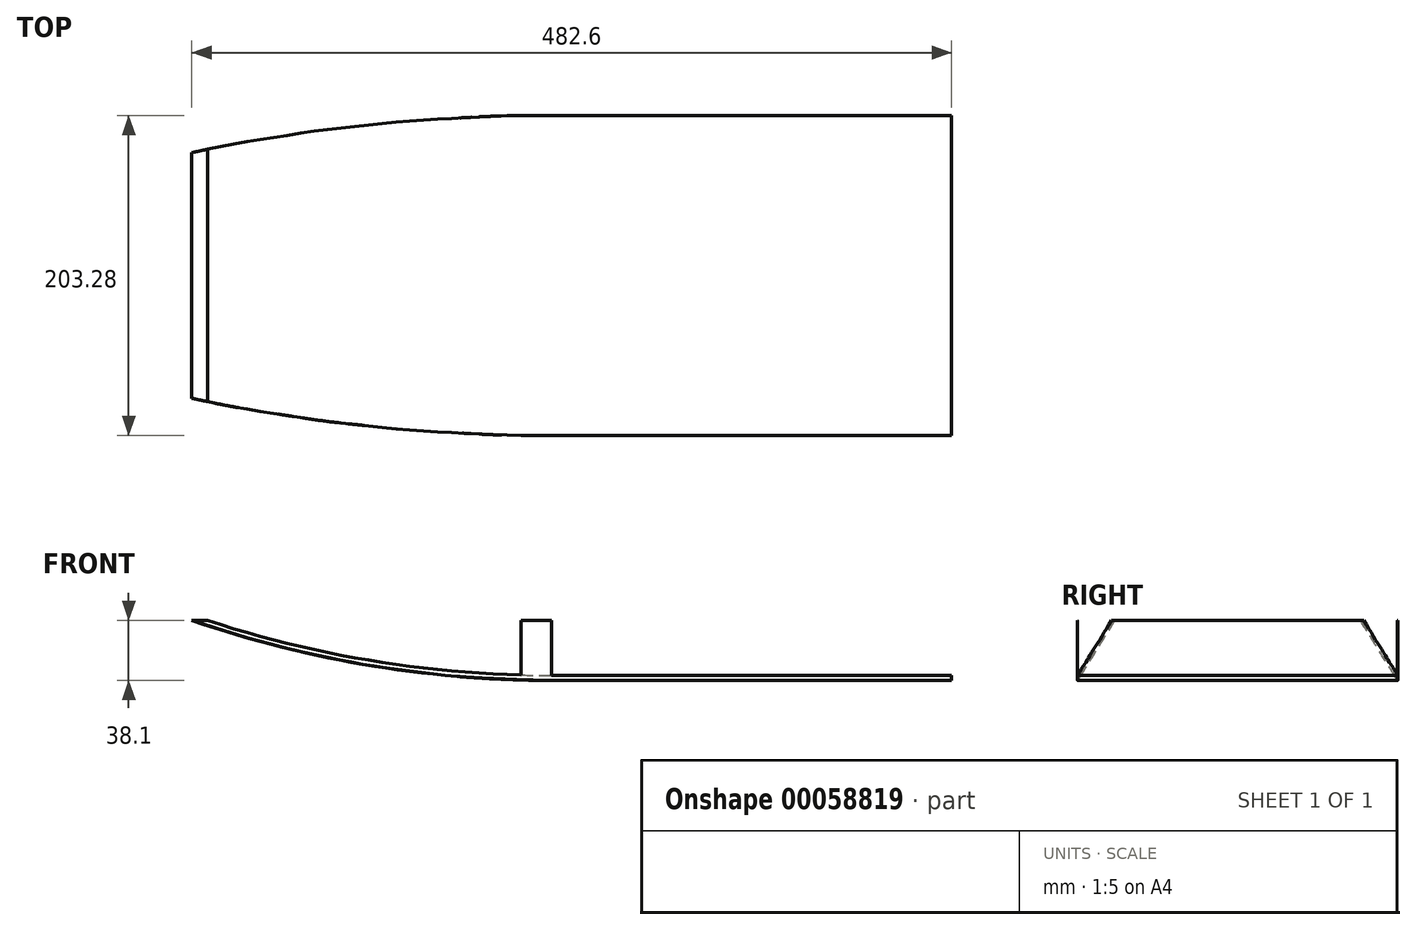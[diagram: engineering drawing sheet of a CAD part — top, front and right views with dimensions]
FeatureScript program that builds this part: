
annotation { "Feature Type Name" : "Feature", "Feature Type Description" : "" }
export const myFeature = defineFeature(function(context is Context, id is Id, definition is map)
    precondition{}
    {
        {
            var Q0;
            Q0=qCreatedBy(makeId("Front.planeOp"),FACE);
            var sketch = newSketch(context, id + "F0", { "sketchPlane" : qUnion([Q0])});
            skLineSegment(sketch, "E0.bottom", {"start": v(0, 0) * mm, "end": v(254, 0) * mm});
            skLineSegment(sketch, "E0.right", {"start": v(254, 0) * mm, "end": v(254, 38.1) * mm});
            skLineSegment(sketch, "E1", {"start": v(254, 38.1) * mm, "end": v(-228.6, 38.1) * mm});
            skArc(sketch, "E2", {"start": v(0, 0) * mm, "mid": v(-115.88, 9.6) * mm, "end": v(-228.6, 38.1) * mm});
            skSolve(sketch);
        }
        {
            var Q0;
            Q0=makeQuery(id+"F0.imprint","IMPRINT",FACE,{"disambiguationData":[TD([[makeQuery(id+"F0.imprint","IMPRINT",EDGE,{"derivedFrom":sQuery(id+"F0.wireOp",EDGE,"E0.bottom")}),1.0]])]});
            extrude(context, id + "F1", {"entities" : qUnion([Q0]), "depth" : 88.9 * mm});
        }
        {
            var Q0;
            Q0=makeQuery(id+"F1.opExtrude","CAP_FACE",FACE,{"disambiguationData":[OSD([sQuery(id+"F0.wireOp",EDGE,"E0.bottom"),sQuery(id+"F0.wireOp",EDGE,"E0.right"),sQuery(id+"F0.wireOp",EDGE,"E1"),sQuery(id+"F0.wireOp",EDGE,"E2")])],"isStart":false});
            extrude(context, id + "F2", {"entities" : qUnion([Q0]), "operationType" : NewBodyOperationType.ADD, "depth" : 50.8 * mm});
        }
        {
            var Q0;
            {var subQ0=sQuery(id+"F0.wireOp",EDGE,"E1");Q0=makeQuery(id+"F2.boolean.opBoolean","MERGE",FACE,{"derivedFrom":[makeQuery(id+"F1.opExtrude","SWEPT_FACE",FACE,{"disambiguationData":[OSD([subQ0])]}),makeQuery(id+"F2.opExtrude","SWEPT_FACE",FACE,{"disambiguationData":[OSD([subQ0])]})]});}
            var sketch = newSketch(context, id + "F3", { "sketchPlane" : qUnion([Q0])});
            skLineSegment(sketch, "E3", {"start": v(-304.42, -139.7) * mm, "end": v(0, -139.7) * mm});
            skArc(sketch, "E4", {"start": v(-228.6, -114.3) * mm, "mid": v(-115, -133.33) * mm, "end": v(0, -139.7) * mm});
            skLineSegment(sketch, "E5", {"start": v(-304.42, -139.7) * mm, "end": v(-304.42, -114.3) * mm});
            skLineSegment(sketch, "E6", {"start": v(-304.42, -114.3) * mm, "end": v(-228.6, -114.3) * mm});
            skSolve(sketch);
        }
        {
            var Q0;
            Q0=qSketchRegion(id+"F3",true);
            extrude(context, id + "F4", {"entities" : qUnion([Q0]), "operationType" : NewBodyOperationType.REMOVE, "endBound" : BoundingType.THROUGH_ALL, "oppositeDirection" : true, "depth" : 25.4 * mm});
        }
        {
            var Q0;
            Q0=makeQuery(id+"F2.opExtrude","CAP_EDGE",EDGE,{"disambiguationData":[OSD([sQuery(id+"F0.wireOp",EDGE,"E0.bottom")])],"isStart":false});
            chamfer(context, id + "F5", {"entities" : qUnion([Q0]), "width" : 38.1 * mm, "tangentPropagation" : true});
        }
        {
            var Q0;
            Q0=makeQuery(id+"F1.opExtrude","SWEPT_BODY",BODY,{"disambiguationData":[OSD([sQuery(id+"F0.wireOp",EDGE,"E0.bottom"),sQuery(id+"F0.wireOp",EDGE,"E0.right"),sQuery(id+"F0.wireOp",EDGE,"E1"),sQuery(id+"F0.wireOp",EDGE,"E2")])]});
            var Q1;
            Q1=qCreatedBy(makeId("Front.planeOp"),FACE);
            mirror(context, id + "F6", {"operationType" : NewBodyOperationType.ADD, "entities" : qUnion([Q0]), "mirrorPlane" : qUnion([Q1])});
        }
        {
            var Q0;
            Q0=qCreatedBy(makeId("Front.planeOp"),FACE);
            var sketch = newSketch(context, id + "F7", { "sketchPlane" : qUnion([Q0])});
            skLineSegment(sketch, "E7.0.3", {"start": v(254, 3.17) * mm, "end": v(0, 3.17) * mm});
            skArc(sketch, "E8.0", {"start": v(0, 3.18) * mm, "mid": v(-110.7, 11.96) * mm, "end": v(-218.61, 38.1) * mm});
            skPoint(sketch, "E9.orphan", {"position": v(-208.68, 34.93) * mm});
            skPoint(sketch, "E10.orphan", {"position": v(250.83, 3.17) * mm});
            skPoint(sketch, "E11.orphan", {"position": v(0, 38.1) * mm});
            skPoint(sketch, "E12.0.end.orphan", {"position": v(0, 0) * mm});
            skPoint(sketch, "E12.0.start.orphan", {"position": v(254, 0) * mm});
            skPoint(sketch, "E12.1.start.orphan", {"position": v(0, 0) * mm});
            skPoint(sketch, "E13.0.start.orphan", {"position": v(-228.6, 38.1) * mm});
            skLineSegment(sketch, "E14", {"start": v(254, 3.17) * mm, "end": v(254, 38.1) * mm});
            skLineSegment(sketch, "E15", {"start": v(254, 38.1) * mm, "end": v(-218.61, 38.1) * mm});
            skSolve(sketch);
        }
        {
            var Q0;
            Q0 = qSketchRegion(id + "F7", true);
            extrude(context, id + "F8", {"entities" : qUnion([Q0]), "operationType" : NewBodyOperationType.REMOVE, "oppositeDirection" : true, "depth" : 101.6 * mm, "hasSecondDirection" : true, "secondDirectionOppositeDirection" : false, "secondDirectionDepth" : 101.6 * mm});
        }
        {
            var Q0;
            Q0=qCreatedBy(makeId("Top.planeOp"),FACE);
            var sketch = newSketch(context, id + "F9", { "sketchPlane" : qUnion([Q0])});
            skLineSegment(sketch, "E16.0", {"start": v(254, 101.6) * mm, "end": v(0, 101.6) * mm});
            skFitSpline(sketch, "E16.1", {"points": [v(0, 101.6) * mm, v(-19.47, 101.6) * mm, v(-38.92, 101.1) * mm, v(-58.37, 100.08) * mm, v(-77.82, 99.07) * mm, v(-97.24, 97.54) * mm, v(-116.62, 95.52) * mm, v(-135.69, 93.52) * mm, v(-154.69, 91.04) * mm, v(-173.62, 88.07) * mm, v(-192.04, 85.17) * mm, v(-210.37, 81.83) * mm, v(-228.6, 78.02) * mm]});
            skLineSegment(sketch, "E16.2", {"start": v(254, 139.7) * mm, "end": v(254, 101.6) * mm});
            skLineSegment(sketch, "E16.3", {"start": v(254, -101.6) * mm, "end": v(0, -101.6) * mm});
            skFitSpline(sketch, "E16.4", {"points": [v(0, -101.6) * mm, v(-19.43, -101.6) * mm, v(-38.87, -101.1) * mm, v(-58.33, -100.08) * mm, v(-77.83, -99.06) * mm, v(-97.27, -97.54) * mm, v(-116.62, -95.52) * mm, v(-135.32, -93.56) * mm, v(-154, -91.13) * mm, v(-172.63, -88.22) * mm, v(-191.42, -85.29) * mm, v(-210.08, -81.89) * mm, v(-228.6, -78.02) * mm]});
            skLineSegment(sketch, "E16.5", {"start": v(254, -139.7) * mm, "end": v(254, -101.6) * mm});
            skLineSegment(sketch, "E17", {"start": v(254, 139.7) * mm, "end": v(-228.6, 139.7) * mm});
            skLineSegment(sketch, "E18", {"start": v(-228.6, 139.7) * mm, "end": v(-228.6, 78.02) * mm});
            skLineSegment(sketch, "E19", {"start": v(254, -139.7) * mm, "end": v(-228.6, -139.7) * mm});
            skLineSegment(sketch, "E20", {"start": v(-228.6, -139.7) * mm, "end": v(-228.6, -78.02) * mm});
            skSolve(sketch);
        }
        {
            var Q0;
            Q0 = qSketchRegion(id + "F9", true);
            extrude(context, id + "F10", {"entities" : qUnion([Q0]), "operationType" : NewBodyOperationType.REMOVE, "endBound" : BoundingType.THROUGH_ALL, "depth" : 25.4 * mm});
        }
    });
